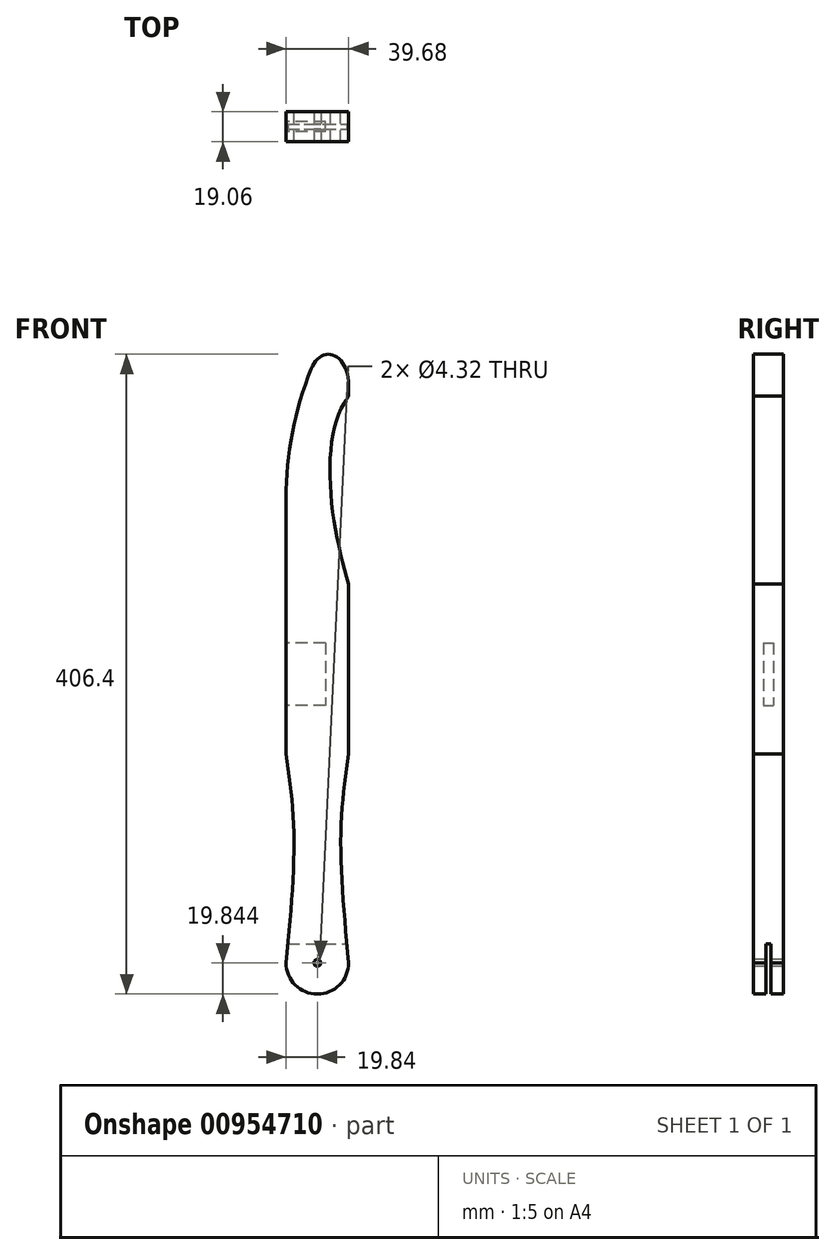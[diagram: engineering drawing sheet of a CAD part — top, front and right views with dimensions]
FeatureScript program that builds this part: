
annotation { "Feature Type Name" : "Feature", "Feature Type Description" : "" }
export const myFeature = defineFeature(function(context is Context, id is Id, definition is map)
    precondition{}
    {
        {
            var Q0;
            Q0=qCreatedBy(makeId("Front.planeOp"),FACE);
            var sketch = newSketch(context, id + "F0", { "sketchPlane" : qUnion([Q0])});
            skLineSegment(sketch, "E0", {"start": v(0, 203.2) * mm, "end": v(0, -203.2) * mm, "construction": true});
            skLineSegment(sketch, "E1", {"start": v(19.84, 0) * mm, "end": v(-19.84, 0) * mm, "construction": true});
            skLineSegment(sketch, "E2.bottom", {"start": v(-19.84, 203.2) * mm, "end": v(19.84, 203.2) * mm});
            skLineSegment(sketch, "E2.top", {"start": v(-19.84, -203.2) * mm, "end": v(19.84, -203.2) * mm});
            skLineSegment(sketch, "E2.left", {"start": v(-19.84, 203.2) * mm, "end": v(-19.84, -203.2) * mm});
            skLineSegment(sketch, "E2.right", {"start": v(19.84, 203.2) * mm, "end": v(19.84, -203.2) * mm});
            skSolve(sketch);
        }
        {
            var Q0;
            Q0 = qSketchRegion(id + "F0", true);
            extrude(context, id + "F1", {"entities" : qUnion([Q0]), "endBound" : BoundingType.SYMMETRIC, "depth" : 19.05 * mm, "offsetDistance" : 25 * mm});
        }
        {
            var Q0;
            Q0=makeQuery(id+"F1.opExtrude","SWEPT_FACE",FACE,{"disambiguationData":[OSD([sQuery(id+"F0.wireOp",EDGE,"E2.left")])]});
            var sketch = newSketch(context, id + "F2", { "sketchPlane" : qUnion([Q0])});
            skLineSegment(sketch, "E3.0", {"start": v(9.53, 203.2) * mm, "end": v(9.53, -203.2) * mm});
            skLineSegment(sketch, "E4.0", {"start": v(-9.53, 203.2) * mm, "end": v(-9.53, -203.2) * mm});
            skLineSegment(sketch, "E5.0", {"start": v(9.53, 203.2) * mm, "end": v(-9.52, 203.2) * mm});
            skLineSegment(sketch, "E6.0", {"start": v(9.53, -203.2) * mm, "end": v(-9.52, -203.2) * mm});
            skLineSegment(sketch, "E7", {"start": v(0, -203.2) * mm, "end": v(0, 203.2) * mm, "construction": true});
            skLineSegment(sketch, "E8", {"start": v(-9.53, 0) * mm, "end": v(9.53, 0) * mm, "construction": true});
            skLineSegment(sketch, "E9.bottom", {"start": v(3.18, 19.84) * mm, "end": v(-3.18, 19.84) * mm});
            skLineSegment(sketch, "E9.top", {"start": v(3.18, -19.84) * mm, "end": v(-3.18, -19.84) * mm});
            skLineSegment(sketch, "E9.left", {"start": v(3.17, 19.84) * mm, "end": v(3.18, -19.84) * mm});
            skLineSegment(sketch, "E9.right", {"start": v(-3.17, 19.84) * mm, "end": v(-3.18, -19.84) * mm});
            skSolve(sketch);
        }
        {
            var Q0;
            Q0=makeQuery(id+"F2.imprint","IMPRINT",FACE,{"disambiguationData":[TD([[makeQuery(id+"F2.imprint","IMPRINT",EDGE,{"derivedFrom":sQuery(id+"F2.wireOp",EDGE,"E9.bottom")}),1.0]])]});
            extrude(context, id + "F3", {"entities" : qUnion([Q0]), "operationType" : NewBodyOperationType.REMOVE, "oppositeDirection" : true, "depth" : 25 * mm, "offsetDistance" : 25 * mm});
        }
        {
            var Q0;
            Q0=makeQuery(id+"F1.opExtrude","CAP_FACE",FACE,{"disambiguationData":[OSD([sQuery(id+"F0.wireOp",EDGE,"E2.bottom"),sQuery(id+"F0.wireOp",EDGE,"E2.top"),sQuery(id+"F0.wireOp",EDGE,"E2.left"),sQuery(id+"F0.wireOp",EDGE,"E2.right")])],"isStart":false});
            var sketch = newSketch(context, id + "F4", { "sketchPlane" : qUnion([Q0])});
            skLineSegment(sketch, "E10.0", {"start": v(-19.84, 203.2) * mm, "end": v(-19.84, -203.2) * mm});
            skLineSegment(sketch, "E11.0.0", {"start": v(-19.84, 19.84) * mm, "end": v(-19.84, -19.84) * mm});
            skLineSegment(sketch, "E12", {"start": v(0, 203.2) * mm, "end": v(0, -203.2) * mm, "construction": true});
            skEllipticalArc(sketch, "E13", {});
            skArc(sketch, "E14", {"start": v(-3.97, 193.9) * mm, "mid": v(-15.84, 153.46) * mm, "end": v(-19.84, 111.52) * mm});
            skLineSegment(sketch, "E15", {"start": v(0, 203.2) * mm, "end": v(0, 120) * mm, "construction": true});
            skLineSegment(sketch, "E16", {"start": v(0, 0) * mm, "end": v(0, 203.2) * mm, "construction": true});
            skLineSegment(sketch, "E17", {"start": v(0, 101.6) * mm, "end": v(19.84, 101.6) * mm, "construction": true});
            skLineSegment(sketch, "E18", {"start": v(0, 101.6) * mm, "end": v(0, 203.2) * mm, "construction": true});
            skLineSegment(sketch, "E19", {"start": v(0, 152.4) * mm, "end": v(19.84, 152.4) * mm, "construction": true});
            skFitSpline(sketch, "E20", {"points": [v(19.84, 176.57) * mm, v(9.92, 152.4) * mm, v(9.92, 101.6) * mm, v(19.84, 57.13) * mm], "startDerivative": vector(-46.96, -64.22) * mm, "endDerivative": vector(30.96, -112.37) * mm});
            skArc(sketch, "E21", {"start": v(-19.84, -183.36) * mm, "mid": v(0, -203.2) * mm, "end": v(19.84, -183.36) * mm});
            skLineSegment(sketch, "E22", {"start": v(0, 0) * mm, "end": v(0, -203.2) * mm, "construction": true});
            skLineSegment(sketch, "E23", {"start": v(0, -101.6) * mm, "end": v(19.84, -101.6) * mm, "construction": true});
            skLineSegment(sketch, "E24", {"start": v(9.92, -101.6) * mm, "end": v(19.84, -101.6) * mm, "construction": true});
            skLineSegment(sketch, "E25", {"start": v(14.88, -101.6) * mm, "end": v(19.84, -101.6) * mm, "construction": true});
            skFitSpline(sketch, "E26", {"points": [v(19.84, -50.8) * mm, v(14.88, -101.6) * mm, v(19.84, -183.36) * mm], "startDerivative": vector(-15.68, -108.28) * mm, "endDerivative": vector(14.5, -155) * mm});
            skFitSpline(sketch, "E27.MirrorCS", {"points": [v(-19.84, -50.8) * mm, v(-14.88, -101.6) * mm, v(-19.84, -183.36) * mm], "startDerivative": vector(15.68, -108.28) * mm, "endDerivative": vector(-14.5, -155) * mm});
            skPoint(sketch, "E28.trimOffspring.end.orphan", {"position": v(0, 19.84) * mm});
            skPoint(sketch, "E29.center.orphan", {"position": v(0, 50.8) * mm});
            skPoint(sketch, "E11.0.3.start.orphan", {"position": v(5.16, 19.84) * mm});
            skPoint(sketch, "E11.0.1.end.orphan", {"position": v(5.16, -19.84) * mm});
            skLineSegment(sketch, "E30", {"start": v(0, -101.6) * mm, "end": v(0, 0) * mm, "construction": true});
            skLineSegment(sketch, "E31", {"start": v(0, -50.8) * mm, "end": v(0, 0) * mm, "construction": true});
            const initialGuessF4  = {"E13": [0.0070341385432274185, 0.18415, 0, 1, 0.01905, 0.012809611456772587, 4.013957300370935, 1.0339490893710863]};
            skSetInitialGuess(sketch, initialGuessF4);
            skSolve(sketch);
        }
        {
            var Q0;
            {var subQ0=sQuery(id+"F4.wireOp",EDGE,"E20");var subQ1=makeQuery(id+"F1.opExtrude","CAP_EDGE",EDGE,{"disambiguationData":[OSD([sQuery(id+"F0.wireOp",EDGE,"E2.right")])],"isStart":false});var subQ2=makeQuery(id+"F4.imprint","INTERSECT",VERTEX,{"disambiguationData":[OD(0.0)],"derivedFrom":[subQ1,subQ0]});Q0=makeQuery(id+"F4.imprint","IMPRINT",FACE,{"disambiguationData":[TD([[makeQuery(id+"F4.imprint","IMPRINT",EDGE,{"disambiguationData":[TD([[subQ2,-1.0]])],"derivedFrom":subQ0}),1.0]])]});}
            var Q1;
            {var subQ0=sQuery(id+"F4.wireOp",EDGE,"E10.0");var subQ1=makeQuery(id+"F1.opExtrude","CAP_EDGE",EDGE,{"disambiguationData":[OSD([sQuery(id+"F0.wireOp",EDGE,"E2.bottom")])],"isStart":false});var subQ2=makeQuery(id+"F4.imprint","INTERSECT",VERTEX,{"derivedFrom":[subQ1,subQ0]});Q1=makeQuery(id+"F4.imprint","IMPRINT",FACE,{"disambiguationData":[TD([[makeQuery(id+"F4.imprint","IMPRINT",EDGE,{"disambiguationData":[TD([[subQ2,-1.0]])],"derivedFrom":subQ0}),1.0]])]});}
            var Q2;
            {var subQ0=sQuery(id+"F4.wireOp",EDGE,"E13");var subQ1=makeQuery(id+"F1.opExtrude","CAP_EDGE",EDGE,{"disambiguationData":[OSD([sQuery(id+"F0.wireOp",EDGE,"E2.bottom")])],"isStart":false});var subQ2=makeQuery(id+"F4.imprint","INTERSECT",VERTEX,{"derivedFrom":[subQ1,subQ0]});Q2=makeQuery(id+"F4.imprint","IMPRINT",FACE,{"disambiguationData":[TD([[makeQuery(id+"F4.imprint","IMPRINT",EDGE,{"disambiguationData":[TD([[subQ2,1.0]])],"derivedFrom":subQ0}),-1.0]])]});}
            var Q3;
            {var subQ0=sQuery(id+"F4.wireOp",EDGE,"E14");var subQ1=sQuery(id+"F4.wireOp",EDGE,"E13");var subQ2=makeQuery(id+"F4.imprint","INTERSECT",VERTEX,{"derivedFrom":[subQ1,subQ0]});Q3=makeQuery(id+"F4.imprint","IMPRINT",FACE,{"disambiguationData":[TD([[makeQuery(id+"F4.imprint","IMPRINT",EDGE,{"disambiguationData":[TD([[subQ2,1.0]])],"derivedFrom":subQ1}),-1.0]])]});}
            var Q4;
            {var subQ0=sQuery(id+"F4.wireOp",EDGE,"E26");var subQ1=sQuery(id+"F4.wireOp",EDGE,"E21");var subQ4=makeQuery(id+"F4.imprint","INTERSECT",VERTEX,{"derivedFrom":[subQ1,subQ0]});Q4=makeQuery(id+"F4.imprint","IMPRINT",FACE,{"disambiguationData":[TD([[makeQuery(id+"F4.imprint","IMPRINT",EDGE,{"disambiguationData":[TD([[subQ4,1.0]])],"derivedFrom":subQ0}),1.0]])]});}
            var Q5;
            {var subQ0=sQuery(id+"F4.wireOp",EDGE,"E27.MirrorCS");var subQ4=sQuery(id+"F4.wireOp",EDGE,"E21");var subQ7=makeQuery(id+"F4.imprint","INTERSECT",VERTEX,{"derivedFrom":[subQ4,subQ0]});Q5=makeQuery(id+"F4.imprint","IMPRINT",FACE,{"disambiguationData":[TD([[makeQuery(id+"F4.imprint","IMPRINT",EDGE,{"disambiguationData":[TD([[subQ7,1.0]])],"derivedFrom":subQ0}),-1.0]])]});}
            var Q6;
            {var subQ1=makeQuery(id+"F1.opExtrude","CAP_EDGE",EDGE,{"disambiguationData":[OSD([sQuery(id+"F0.wireOp",EDGE,"E2.right")])],"isStart":false});var subQ3=makeQuery(id+"F1.opExtrude","CAP_EDGE",EDGE,{"disambiguationData":[OSD([sQuery(id+"F0.wireOp",EDGE,"E2.top")])],"isStart":false});var subQ5=makeQuery(id+"F4.imprint","INTERSECT",VERTEX,{"derivedFrom":[subQ3,subQ1]});Q6=makeQuery(id+"F4.imprint","IMPRINT",FACE,{"disambiguationData":[TD([[makeQuery(id+"F4.imprint","IMPRINT",EDGE,{"disambiguationData":[TD([[subQ5,1.0]])],"derivedFrom":subQ3}),1.0]])]});}
            var Q7;
            {var subQ0=sQuery(id+"F4.wireOp",EDGE,"E10.0");var subQ1=makeQuery(id+"F1.opExtrude","CAP_EDGE",EDGE,{"disambiguationData":[OSD([sQuery(id+"F0.wireOp",EDGE,"E2.top")])],"isStart":false});var subQ2=makeQuery(id+"F4.imprint","INTERSECT",VERTEX,{"derivedFrom":[subQ1,subQ0]});Q7=makeQuery(id+"F4.imprint","IMPRINT",FACE,{"disambiguationData":[TD([[makeQuery(id+"F4.imprint","IMPRINT",EDGE,{"disambiguationData":[TD([[subQ2,-1.0]])],"derivedFrom":subQ1}),1.0]])]});}
            extrude(context, id + "F5", {"entities" : qUnion([Q0, Q1, Q2, Q3, Q4, Q5, Q6, Q7]), "operationType" : NewBodyOperationType.REMOVE, "endBound" : BoundingType.THROUGH_ALL, "oppositeDirection" : true, "depth" : 25 * mm, "offsetDistance" : 25 * mm});
        }
        {
            var Q0;
            Q0=qCreatedBy(makeId("Front.planeOp"),FACE);
            var sketch = newSketch(context, id + "F6", { "sketchPlane" : qUnion([Q0])});
            skLineSegment(sketch, "E32", {"start": v(0, 203.2) * mm, "end": v(0, -203.2) * mm, "construction": true});
            skLineSegment(sketch, "E33", {"start": v(-40.94, 0) * mm, "end": v(40.94, 0) * mm, "construction": true});
            skArc(sketch, "E34", {"start": v(-15.87, -171.45) * mm, "mid": v(0, -203.2) * mm, "end": v(15.88, -171.45) * mm});
            skLineSegment(sketch, "E35", {"start": v(-15.87, -171.45) * mm, "end": v(15.88, -171.45) * mm});
            skLineSegment(sketch, "E36.bottom", {"start": v(-19.84, -171.45) * mm, "end": v(19.84, -171.45) * mm});
            skLineSegment(sketch, "E36.top", {"start": v(-19.84, -203.2) * mm, "end": v(19.84, -203.2) * mm});
            skLineSegment(sketch, "E36.left", {"start": v(-19.84, -171.45) * mm, "end": v(-19.84, -203.2) * mm});
            skLineSegment(sketch, "E36.right", {"start": v(19.84, -171.45) * mm, "end": v(19.84, -203.2) * mm});
            skSolve(sketch);
        }
        {
            var Q0;
            Q0 = qSketchRegion(id + "F6", true);
            extrude(context, id + "F7", {"entities" : qUnion([Q0]), "operationType" : NewBodyOperationType.REMOVE, "endBound" : BoundingType.SYMMETRIC, "depth" : 3.17 * mm, "offsetDistance" : 25.4 * mm});
        }
        {
            var Q0;
            Q0=makeQuery(id+"F1.opExtrude","CAP_FACE",FACE,{"disambiguationData":[OSD([sQuery(id+"F0.wireOp",EDGE,"E2.bottom"),sQuery(id+"F0.wireOp",EDGE,"E2.top"),sQuery(id+"F0.wireOp",EDGE,"E2.left"),sQuery(id+"F0.wireOp",EDGE,"E2.right")])],"isStart":false});
            var sketch = newSketch(context, id + "F8", { "sketchPlane" : qUnion([Q0])});
            skFitSpline(sketch, "E37.0.0", {"points": [v(-19.84, -50.8) * mm, v(-17.54, -66.72) * mm, v(-12.3, -102.82) * mm, v(-17.14, -154.48) * mm, v(-19.84, -183.36) * mm]});
            skArc(sketch, "E37.0.1", {"start": v(-19.84, -183.36) * mm, "mid": v(0, -203.2) * mm, "end": v(19.84, -183.36) * mm});
            skFitSpline(sketch, "E37.0.2", {"points": [v(19.84, -183.36) * mm, v(17.14, -154.48) * mm, v(12.3, -102.82) * mm, v(17.54, -66.72) * mm, v(19.84, -50.8) * mm]});
            skLineSegment(sketch, "E37.0.3", {"start": v(19.84, -50.8) * mm, "end": v(19.84, 57.13) * mm});
            skFitSpline(sketch, "E37.0.4", {"points": [v(19.84, 57.13) * mm, v(16.18, 70.45) * mm, v(7.95, 100.85) * mm, v(6.8, 151.59) * mm, v(15.63, 170.8) * mm, v(19.84, 176.57) * mm]});
            skEllipticalArc(sketch, "E37.0.5", {});
            skArc(sketch, "E37.0.6", {"start": v(-3.97, 193.9) * mm, "mid": v(-15.84, 153.46) * mm, "end": v(-19.84, 111.52) * mm});
            skLineSegment(sketch, "E37.0.7", {"start": v(-19.84, 111.52) * mm, "end": v(-19.84, -50.8) * mm});
            const initialGuessF8  = {"E37.0.5": [0.0070341385432274185, 0.18415, 0, 1, 0.01905, 0.012809611456772587, 4.013957300370935, 1.0339490893710863]};
            skSetInitialGuess(sketch, initialGuessF8);
            skSolve(sketch);
        }
        {
            var Q0;
            Q0=sQuery(id+"F8.wireOp",VERTEX,"E37.0.1.center");
            var Q1;
            Q1=makeQuery(id+"F1.opExtrude","SWEPT_BODY",BODY,{"disambiguationData":[OSD([sQuery(id+"F0.wireOp",EDGE,"E2.bottom"),sQuery(id+"F0.wireOp",EDGE,"E2.top"),sQuery(id+"F0.wireOp",EDGE,"E2.left"),sQuery(id+"F0.wireOp",EDGE,"E2.right")])]});
            hole(context, id + "F9", {"style" : HoleStyle.SIMPLE, "endStyle" : HoleEndStyle.THROUGH, "standardTappedOrClearance" : lookupTablePath({ "fit" : "Normal (ASME)", "standard" : "ANSI", "size" : "#6", "type" : "Clearance" }), "standardBlindInLast" : lookupTablePath({ "fit" : "Normal", "standard" : "ANSI", "engagement" : "75%", "pitch" : "32 tpi", "size" : "#6", "type" : "Clearance & tapped" }), "holeDiameter" : 4.32 * mm, "majorDiameter" : 6.35 * mm, "isTappedThrough" : true, "tappedDepth" : 12.7 * mm, "tapClearance" : 3, "startFromSketch" : true, "locations" : qUnion([Q0]), "scope" : qUnion([Q1])});
        }
    });
